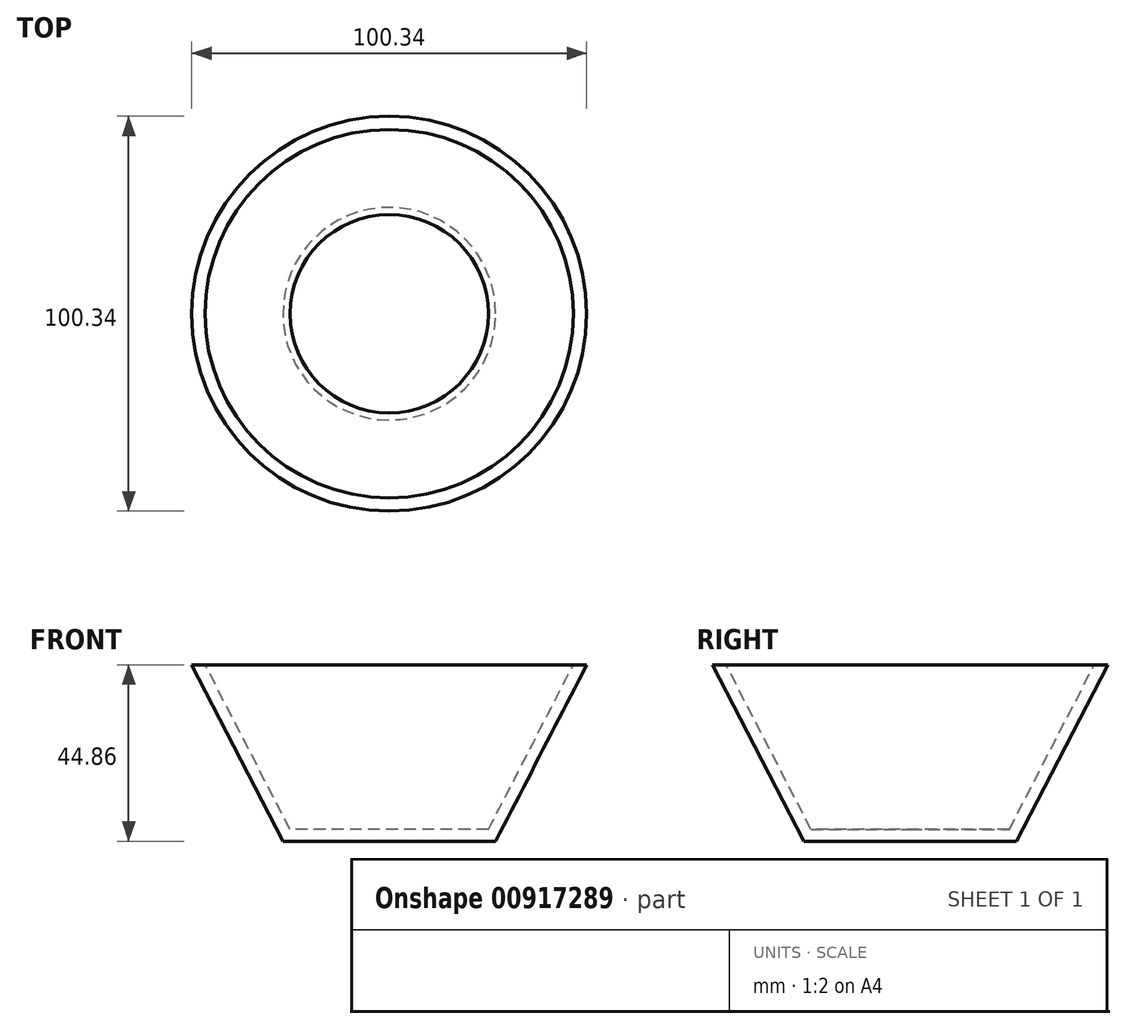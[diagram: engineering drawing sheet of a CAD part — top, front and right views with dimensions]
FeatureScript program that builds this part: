
annotation { "Feature Type Name" : "Feature", "Feature Type Description" : "" }
export const myFeature = defineFeature(function(context is Context, id is Id, definition is map)
    precondition{}
    {
        {
            var Q0;
            Q0=qCreatedBy(makeId("Front.planeOp"),FACE);
            var sketch = newSketch(context, id + "F0", { "sketchPlane" : qUnion([Q0])});
            skLineSegment(sketch, "E0", {"start": v(-157.53, 48.48) * mm, "end": v(-157.53, 44.14) * mm});
            skLineSegment(sketch, "E1", {"start": v(-157.53, 44.14) * mm, "end": v(-157.53, 3.62) * mm});
            skLineSegment(sketch, "E2", {"start": v(-157.53, 3.62) * mm, "end": v(-130.51, 3.62) * mm});
            skLineSegment(sketch, "E3", {"start": v(-130.51, 3.62) * mm, "end": v(-107.36, 48.48) * mm});
            skLineSegment(sketch, "E4", {"start": v(-107.36, 48.48) * mm, "end": v(-157.53, 48.48) * mm});
            skSolve(sketch);
        }
        {
            var Q0;
            Q0 = qSketchRegion(id + "F0", true);
            var Q1;
            Q1=sQuery(id+"F0.wireOp",EDGE,"E1");
            revolve(context, id + "F1", {"surfaceOperationType" : NewSurfaceOperationType.NEW, "entities" : qUnion([Q0]), "axis" : qUnion([Q1]), "revolveType" : RevolveType.FULL});
        }
        {
            var Q0;
            Q0=makeQuery(id+"F1.opRevolve","SWEPT_FACE",FACE,{"disambiguationData":[OSD([sQuery(id+"F0.wireOp",EDGE,"E4")])]});
            shell(context, id + "F2", {"entities" : qUnion([Q0]), "thickness" : 3 * mm});
        }
    });
